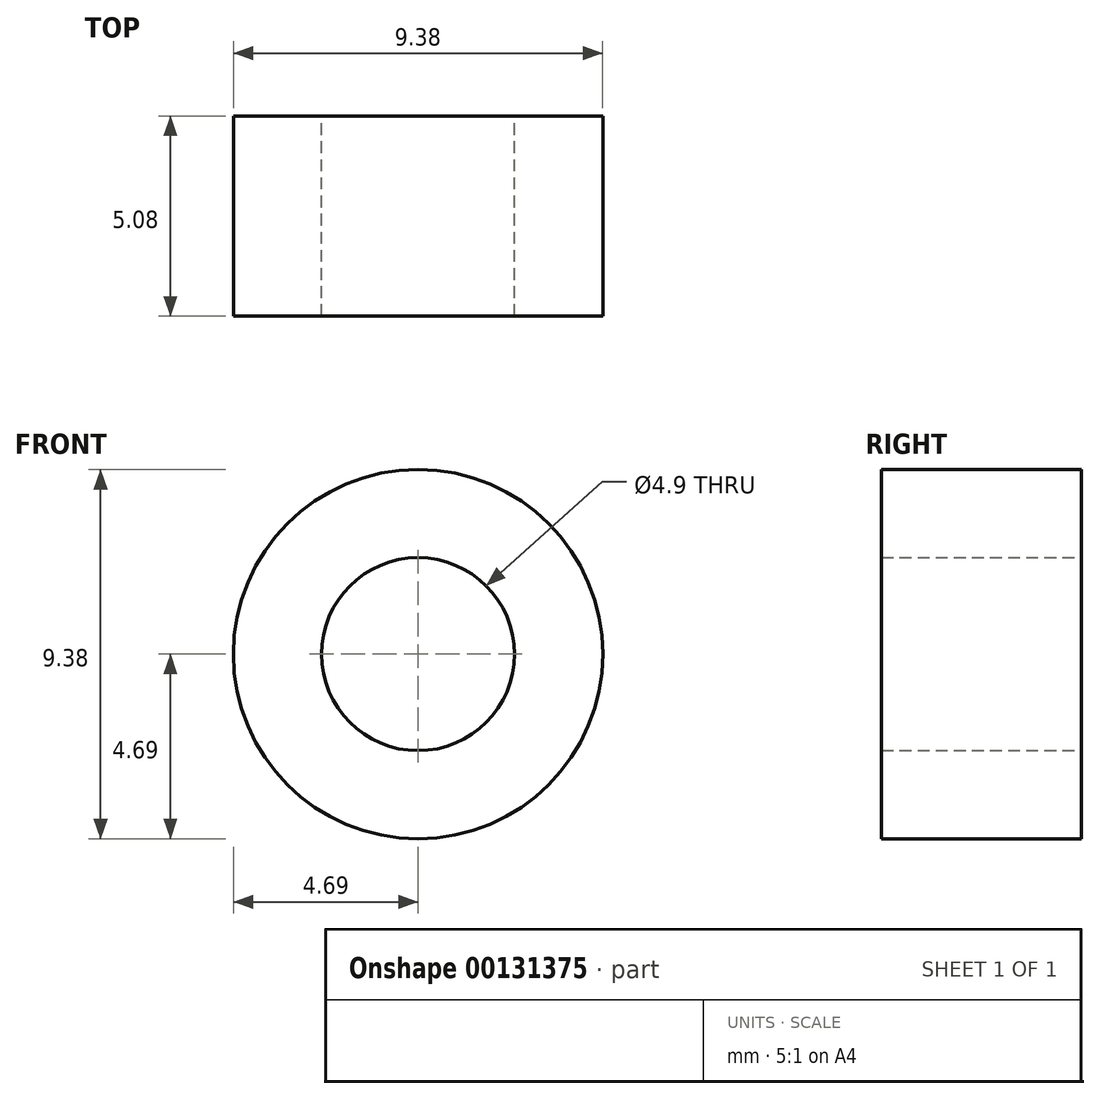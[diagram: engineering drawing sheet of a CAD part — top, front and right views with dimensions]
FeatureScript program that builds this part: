
annotation { "Feature Type Name" : "Feature", "Feature Type Description" : "" }
export const myFeature = defineFeature(function(context is Context, id is Id, definition is map)
    precondition{}
    {
        {
            var Q0;
            Q0=qCreatedBy(makeId("Front.planeOp"),FACE);
            var sketch = newSketch(context, id + "F0", { "sketchPlane" : qUnion([Q0])});
            skCircle(sketch, "E0", {"center": v(0, 0) * mm, "radius": 4.7 * mm});
            skSolve(sketch);
        }
        {
            var Q0;
            Q0 = qSketchRegion(id + "F0", true);
            extrude(context, id + "F1", {"entities" : qUnion([Q0]), "depth" : 5.08 * mm});
        }
        {
            var Q0;
            Q0=qCreatedBy(makeId("Front.planeOp"),FACE);
            var sketch = newSketch(context, id + "F2", { "sketchPlane" : qUnion([Q0])});
            skPoint(sketch, "E1", {"position": v(0, 0) * mm});
            skCircle(sketch, "E2", {"center": v(0, 0) * mm, "radius": 2.45 * mm});
            skSolve(sketch);
        }
        {
            var Q0;
            Q0 = qSketchRegion(id + "F2", true);
            extrude(context, id + "F3", {"entities" : qUnion([Q0]), "operationType" : NewBodyOperationType.REMOVE, "depth" : 25.4 * mm});
        }
    });
